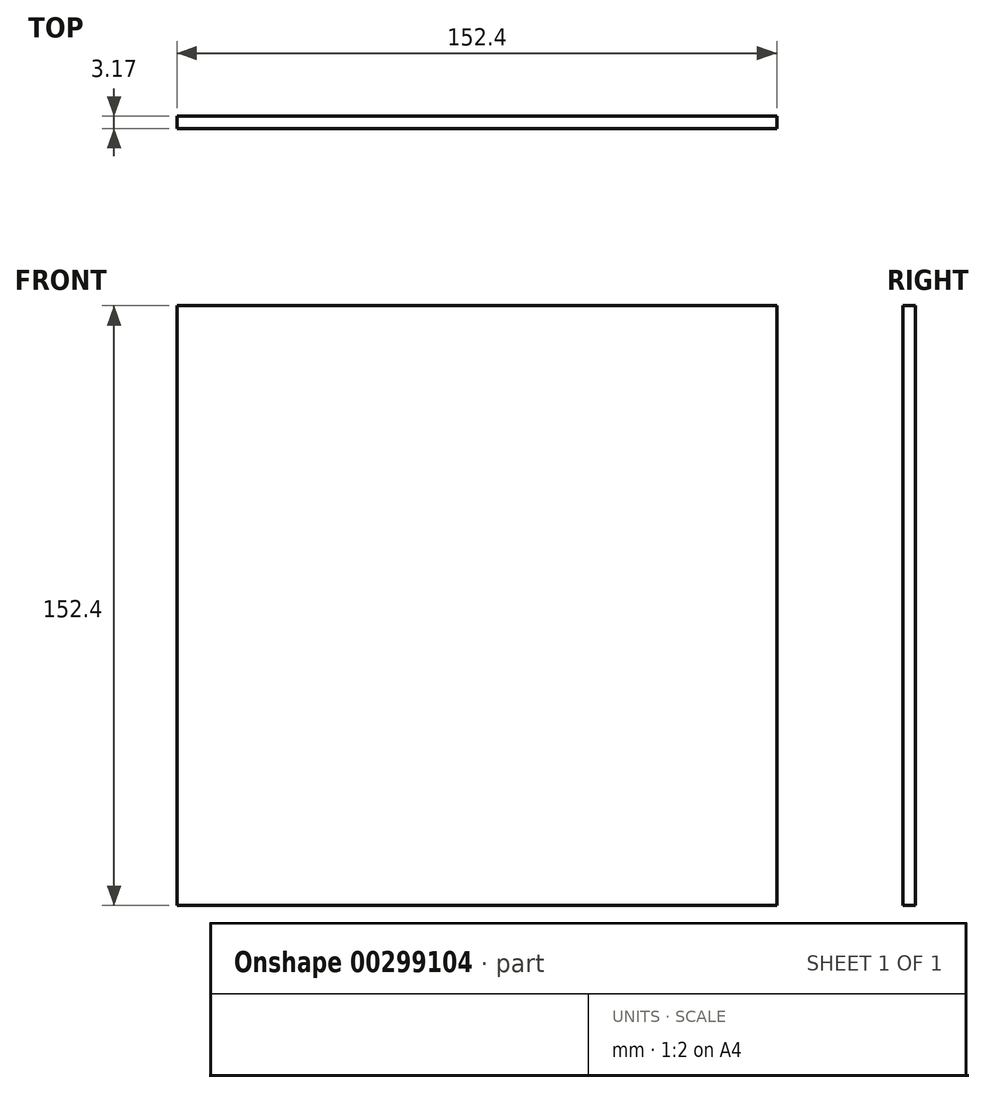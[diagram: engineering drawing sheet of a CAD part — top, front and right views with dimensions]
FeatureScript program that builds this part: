
annotation { "Feature Type Name" : "Feature", "Feature Type Description" : "" }
export const myFeature = defineFeature(function(context is Context, id is Id, definition is map)
    precondition{}
    {
        {
            var Q0;
            Q0=qCreatedBy(makeId("Front.planeOp"),FACE);
            var sketch = newSketch(context, id + "F0", { "sketchPlane" : qUnion([Q0])});
            skLineSegment(sketch, "E0.bottom", {"start": v(-76.2, 76.2) * mm, "end": v(76.2, 76.2) * mm});
            skLineSegment(sketch, "E0.top", {"start": v(-76.2, -76.2) * mm, "end": v(76.2, -76.2) * mm});
            skLineSegment(sketch, "E0.left", {"start": v(-76.2, 76.2) * mm, "end": v(-76.2, -76.2) * mm});
            skLineSegment(sketch, "E0.right", {"start": v(76.2, 76.2) * mm, "end": v(76.2, -76.2) * mm});
            skPoint(sketch, "E0.middle", {"position": v(0, 0) * mm});
            skSolve(sketch);
        }
        {
            var Q0;
            Q0 = qSketchRegion(id + "F0", true);
            extrude(context, id + "F1", {"entities" : qUnion([Q0]), "depth" : 3.17 * mm});
        }
    });
